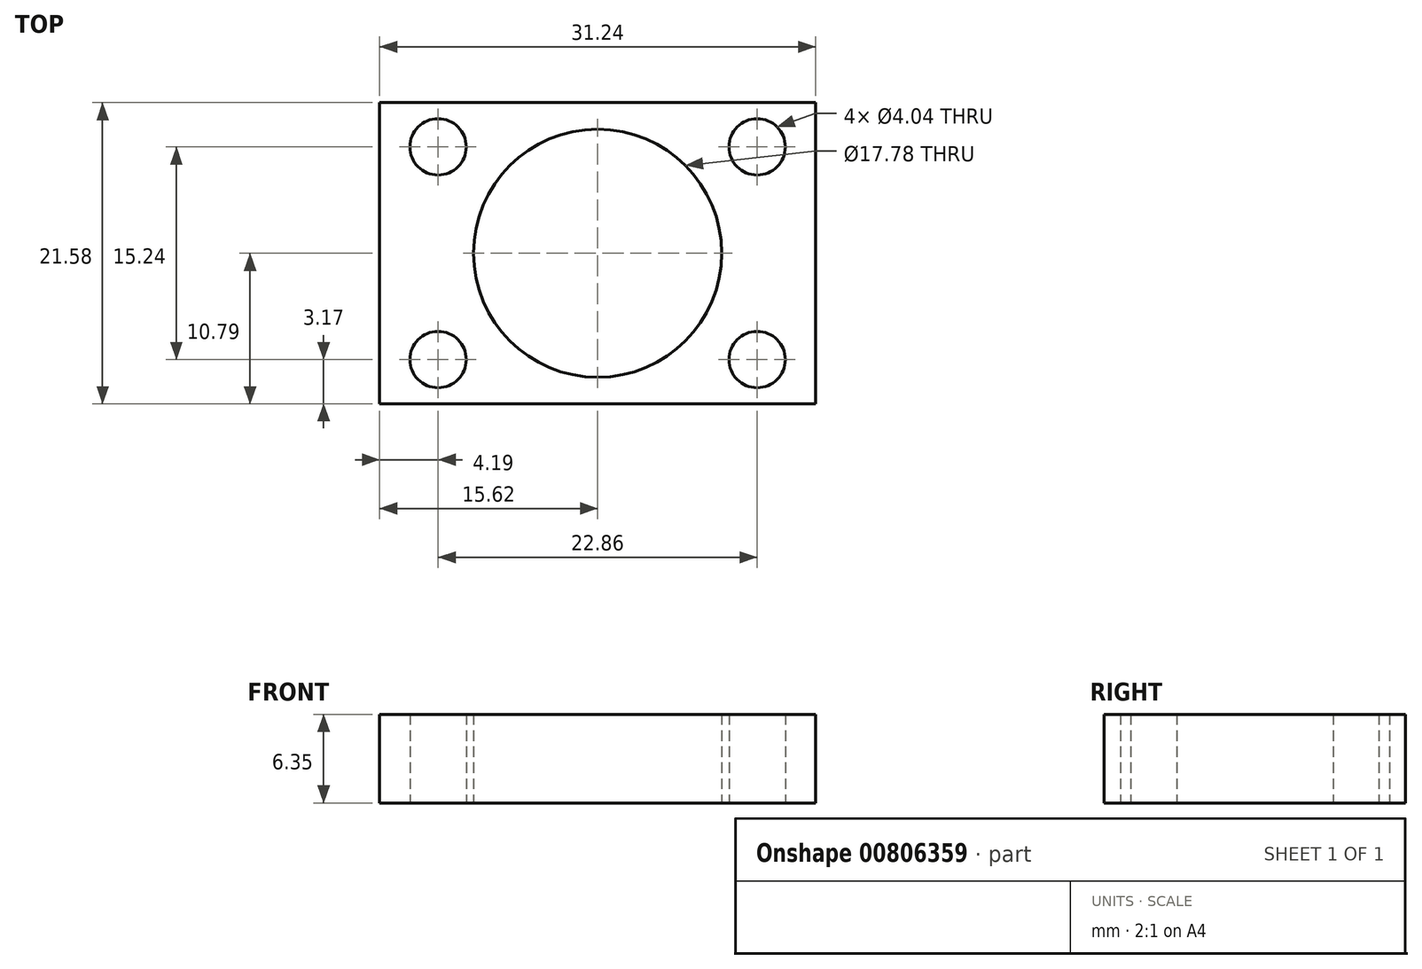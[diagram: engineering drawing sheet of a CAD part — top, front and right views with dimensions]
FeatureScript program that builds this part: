
annotation { "Feature Type Name" : "Feature", "Feature Type Description" : "" }
export const myFeature = defineFeature(function(context is Context, id is Id, definition is map)
    precondition{}
    {
        {
            var Q0;
            Q0=qCreatedBy(makeId("Top.planeOp"),FACE);
            var sketch = newSketch(context, id + "F0", { "sketchPlane" : qUnion([Q0])});
            skLineSegment(sketch, "E0.bottom", {"start": v(15.62, 10.8) * mm, "end": v(-15.62, 10.8) * mm});
            skLineSegment(sketch, "E0.top", {"start": v(15.62, -10.8) * mm, "end": v(-15.62, -10.8) * mm});
            skLineSegment(sketch, "E0.left", {"start": v(15.62, 10.8) * mm, "end": v(15.62, -10.8) * mm});
            skLineSegment(sketch, "E0.right", {"start": v(-15.62, 10.8) * mm, "end": v(-15.62, -10.8) * mm});
            skPoint(sketch, "E0.middle", {"position": v(0, 0) * mm});
            skCircle(sketch, "E1", {"center": v(0, 0) * mm, "radius": 8.9 * mm});
            skCircle(sketch, "E2", {"center": v(-11.43, 7.62) * mm, "radius": 2.02 * mm});
            skCircle(sketch, "E3", {"center": v(-11.43, -7.62) * mm, "radius": 2.02 * mm});
            skCircle(sketch, "E4", {"center": v(11.43, -7.62) * mm, "radius": 2.02 * mm});
            skCircle(sketch, "E5", {"center": v(11.43, 7.62) * mm, "radius": 2.02 * mm});
            skSolve(sketch);
        }
        {
            var Q0;
            Q0 = qSketchRegion(id + "F0", true);
            extrude(context, id + "F1", {"entities" : qUnion([Q0]), "depth" : 6.35 * mm, "offsetDistance" : 25.4 * mm});
        }
    });
